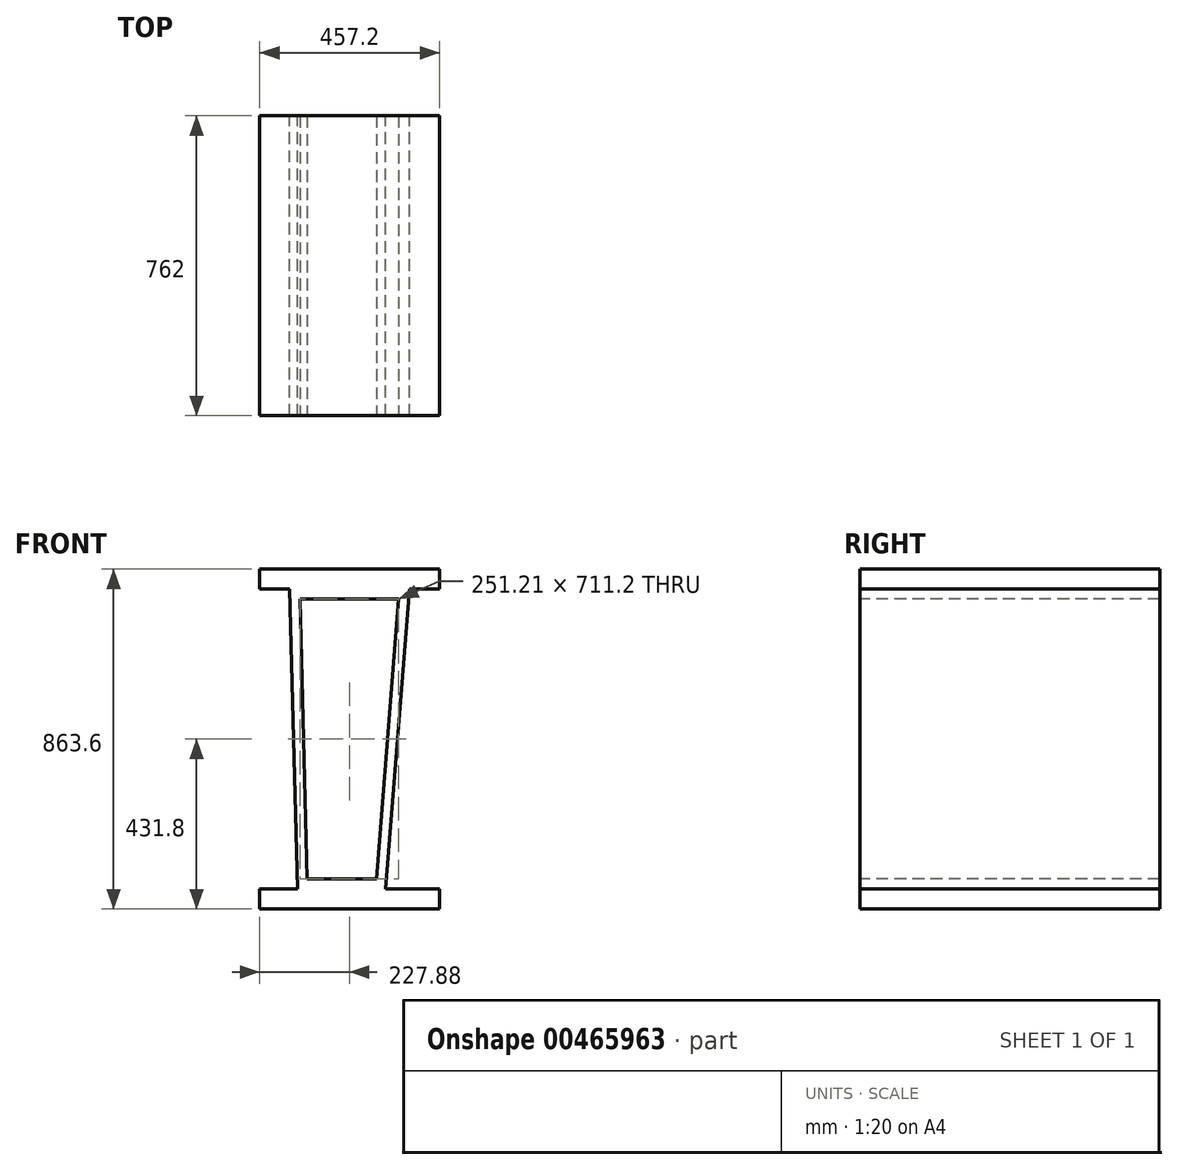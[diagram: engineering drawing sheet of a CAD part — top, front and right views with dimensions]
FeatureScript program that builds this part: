
annotation { "Feature Type Name" : "Feature", "Feature Type Description" : "" }
export const myFeature = defineFeature(function(context is Context, id is Id, definition is map)
    precondition{}
    {
        {
            var Q0;
            Q0=qCreatedBy(makeId("Front.planeOp"),FACE);
            var sketch = newSketch(context, id + "F0", { "sketchPlane" : qUnion([Q0])});
            skLineSegment(sketch, "E0", {"start": v(-228.6, 0) * mm, "end": v(228.6, 0) * mm});
            skLineSegment(sketch, "E1", {"start": v(-228.6, 0) * mm, "end": v(-228.6, -50.8) * mm});
            skLineSegment(sketch, "E2", {"start": v(-228.6, -50.8) * mm, "end": v(228.6, -50.8) * mm});
            skLineSegment(sketch, "E3", {"start": v(228.6, -50.8) * mm, "end": v(228.6, 0) * mm});
            skLineSegment(sketch, "E4", {"start": v(-152.4, -50.8) * mm, "end": v(-132.38, -812.8) * mm});
            skLineSegment(sketch, "E5", {"start": v(-132.38, -812.8) * mm, "end": v(91.36, -812.8) * mm});
            skLineSegment(sketch, "E6", {"start": v(91.36, -812.8) * mm, "end": v(152.4, -50.8) * mm});
            skLineSegment(sketch, "E7.bottom", {"start": v(-228.6, -812.8) * mm, "end": v(228.6, -812.8) * mm});
            skLineSegment(sketch, "E7.top", {"start": v(-228.6, -863.6) * mm, "end": v(228.6, -863.6) * mm});
            skLineSegment(sketch, "E7.left", {"start": v(-228.6, -812.8) * mm, "end": v(-228.6, -863.6) * mm});
            skLineSegment(sketch, "E7.right", {"start": v(228.6, -812.8) * mm, "end": v(228.6, -863.6) * mm});
            skSolve(sketch);
        }
        {
            var Q0;
            Q0=makeQuery(id+"F0.imprint","IMPRINT",FACE,{"disambiguationData":[TD([[makeQuery(id+"F0.imprint","IMPRINT",EDGE,{"derivedFrom":sQuery(id+"F0.wireOp",EDGE,"E0")}),-1.0]])]});
            var Q1;
            {var subQ0=sQuery(id+"F0.wireOp",EDGE,"E4");Q1=makeQuery(id+"F0.imprint","IMPRINT",FACE,{"disambiguationData":[TD([[makeQuery(id+"F0.imprint","IMPRINT",EDGE,{"derivedFrom":subQ0}),1.0]])]});}
            var Q2;
            Q2=makeQuery(id+"F0.imprint","IMPRINT",FACE,{"disambiguationData":[TD([[makeQuery(id+"F0.imprint","IMPRINT",EDGE,{"derivedFrom":sQuery(id+"F0.wireOp",EDGE,"E7.top")}),1.0]])]});
            extrude(context, id + "F1", {"entities" : qUnion([Q0, Q1, Q2]), "depth" : 762 * mm});
        }
        {
            var Q0;
            Q0=makeQuery(id+"F1.opExtrude","CAP_FACE",FACE,{"disambiguationData":[OSD([sQuery(id+"F0.wireOp",EDGE,"E0"),sQuery(id+"F0.wireOp",EDGE,"E1"),sQuery(id+"F0.wireOp",EDGE,"E2"),sQuery(id+"F0.wireOp",EDGE,"E3"),sQuery(id+"F0.wireOp",EDGE,"E4"),sQuery(id+"F0.wireOp",EDGE,"E6"),sQuery(id+"F0.wireOp",EDGE,"E7.bottom"),sQuery(id+"F0.wireOp",EDGE,"E7.top"),sQuery(id+"F0.wireOp",EDGE,"E7.left"),sQuery(id+"F0.wireOp",EDGE,"E7.right")])],"isStart":false});
            var sketch = newSketch(context, id + "F2", { "sketchPlane" : qUnion([Q0])});
            skLineSegment(sketch, "E8", {"start": v(-126.32, -76.2) * mm, "end": v(124.88, -76.2) * mm});
            skLineSegment(sketch, "E9", {"start": v(124.88, -76.2) * mm, "end": v(67.91, -787.4) * mm});
            skLineSegment(sketch, "E10", {"start": v(67.91, -787.4) * mm, "end": v(-107.64, -787.4) * mm});
            skLineSegment(sketch, "E11", {"start": v(-107.64, -787.4) * mm, "end": v(-126.32, -76.2) * mm});
            skSolve(sketch);
        }
        {
            var Q0;
            Q0=makeQuery(id+"F2.imprint","IMPRINT",FACE,{"disambiguationData":[TD([[makeQuery(id+"F2.imprint","IMPRINT",EDGE,{"derivedFrom":sQuery(id+"F2.wireOp",EDGE,"E8")}),-1.0]])]});
            extrude(context, id + "F3", {"entities" : qUnion([Q0]), "operationType" : NewBodyOperationType.REMOVE, "endBound" : BoundingType.THROUGH_ALL, "oppositeDirection" : true, "depth" : 25.4 * mm});
        }
    });
